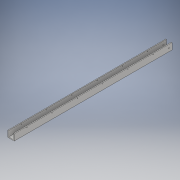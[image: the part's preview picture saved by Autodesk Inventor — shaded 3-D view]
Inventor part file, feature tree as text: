
AUTODESK INVENTOR PART (.ipt)
format: ipt  version: 2018 (Build 220112000, 112)  size: 160,768 bytes
history: native  units: in
note: dims shown in document units (in); Inventor stores cm internally (conversion verified against a paired STEP export)
features: extrude x5, sketch x5
ambient origin geometry x8: Origin, YZ Plane, XZ Plane, XY Plane, X Axis, Y Axis, Z Axis, Center Point
bodies: Solid1 (feature_tree)
feature tree (10):
  extrude  "Extrusion1"  Depth=1.0in
  extrude  "Extrusion2"  Depth=25.0in TaperAngle=0.0deg
  extrude  "Extrusion3"  Depth=0.143in
  extrude  "Extrusion4"  Depth=4.0in
  extrude  "Extrusion6"  Depth=25.0in
  sketch  "Sketch1"  dims[d0=1.0in d1=1.0in]
  sketch  "Sketch2"  dims[d2=0.125in d3=25.0in d4=0.0in]
  sketch  "Sketch3"  dims[d5=0.263in d6=0.143in]
  sketch  "Sketch4"  dims[d8=3.0in d9=4.0in]
  sketch  "Sketch5"  dims[d11=4.0in d12=4.0in d13=4.0in d14=4.0in d15=0.104in d16=25.0in d17=0.0in d18=0.75in d19=25.0in d20=0.0in d21=0.5in d22=180.0deg d23=0.2031in d24=25.0in d25=0.0in d26=0.5in d27=90.0deg d28=0.2031in d31=25.0in d32=0.0in]
